# Revit family: VRIF-4104_2X2_2x4
name_source: partatom
category: Lighting Fixtures
units: mm (PartAtom-declared; Revit-internal decimal feet)

## family parameters
Always vertical = Yes
Cut with Voids When Loaded = No
Host = Ceiling
Light Source = Yes
OmniClass Number = 23.80.70.11.14.17
OmniClass Title = Direct/Indirect
Part Type = Normal
Room Calculation Point = No
Round Connector Dimension = Use Diameter
Shared = No

## types (4) — shared parameters
Color Filter = 16777215
Description = LED Vandal Resistant Recessed Flanged Ceiling Inset Door
Dimming Lamp Color Temperature Shift = <None>
Emit Shape Visible in Rendering = No
Emit from Rectangle Width = 2' - 0 21/32"
Housing Finish = Metal - Viscor - White
Inner Diffuser = Acrylic - Viscor - Frosted Round
Lamp = LED
Lens Flat = Acrylic - Viscor - Clear Lens
Manufacturer = Certolux By Viscor
Model = VRIF-4104
Tilt Angle = 90.00°
URL = https://www.viscor.com
Voltage = 120 V
Width = 2' - 0 21/32"

## per-type parameters (varying)
| type | Apparent Load | Emit from Rectangle Length | Lamp Wattage | Length | Photometric Web File |
| VRIF-4104-2X2-LED840K033LUNV | 33 VA | 2' - 1 5/16" | 33 VA | 2' - 1 5/16" | VRIF-4104-2X2-LED840K033LUNV.ies |
| VRIF-4104-2X4-LED840K039LUNV | 39 VA | 4' - 1 5/16" | 39 VA | 4' - 1 5/16" | VRIF-4104-2X4-LED840K039LUNV.ies |
| VRIF-4104-2X4-LED840K052LUNV | 51 VA | 4' - 1 5/16" | 51 VA | 4' - 1 5/16" | VRIF-4104-2X4-LED840K052LUNV.ies |
| VRIF-4104-2X4-LED840K078LUNV | 75 VA | 4' - 1 5/16" | 75 VA | 4' - 1 5/16" | VRIF-4104-2X4-LED840K078LUNV.ies |

## geometry (parser evidence)
native form markers: Sweep x3
no freeform markers — native parametric forms only
